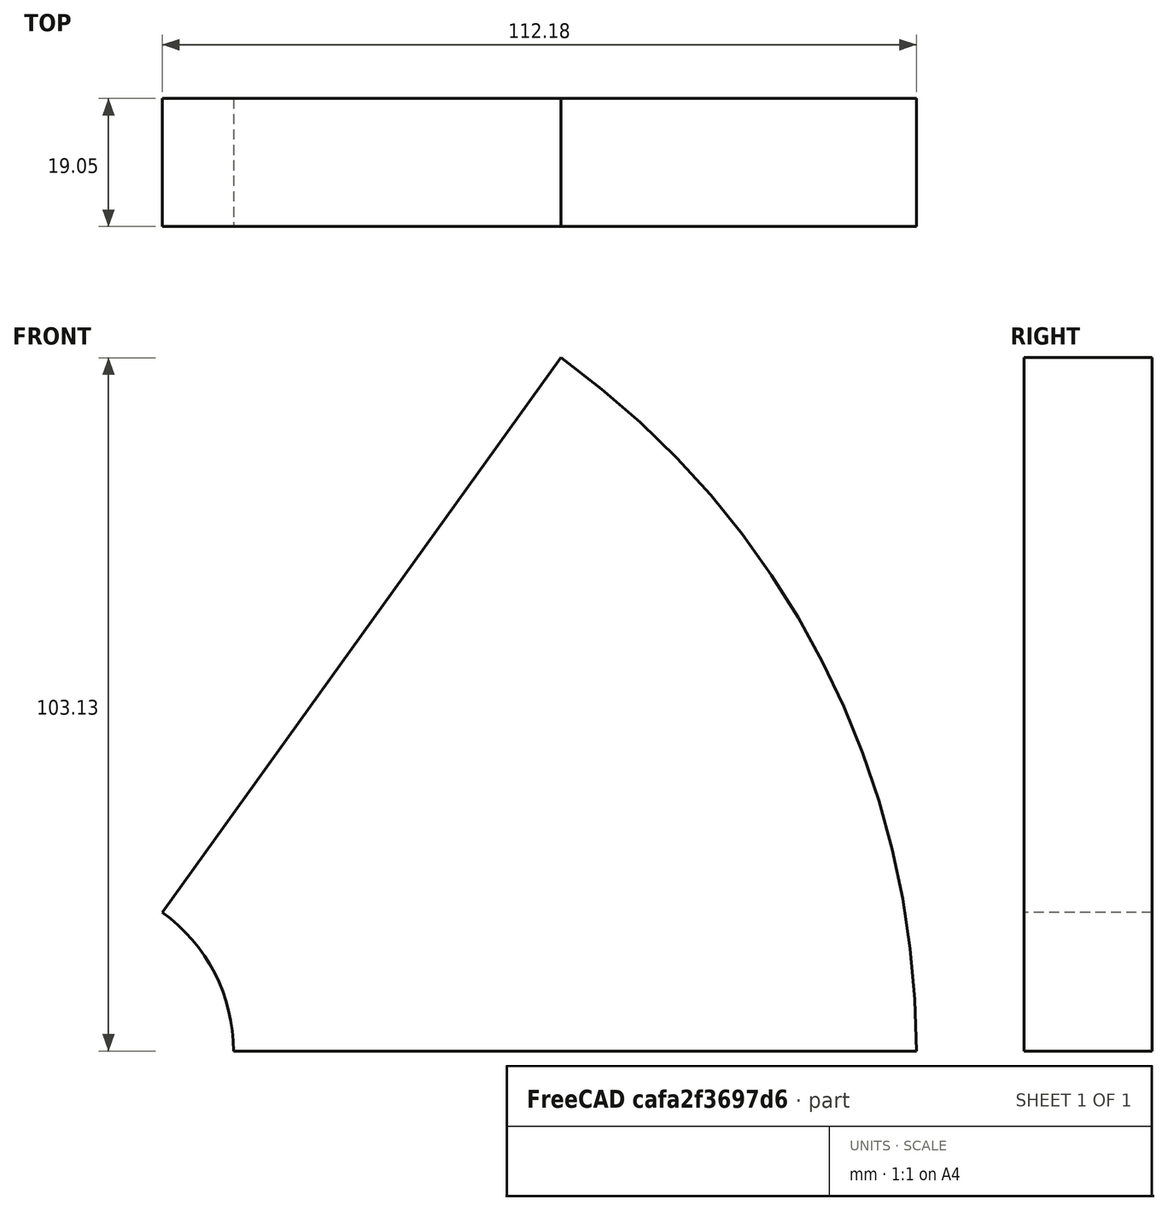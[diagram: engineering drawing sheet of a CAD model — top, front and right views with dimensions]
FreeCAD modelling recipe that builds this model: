
FCSTD DOCUMENT  (FreeCAD 0.19R24291 (Git))
Label: ArcWedge54.24Degrees
License: All rights reserved
LicenseURL: http://en.wikipedia.org/wiki/All_rights_reserved
objects: TechDraw::DrawViewDimension×4, TechDraw::DrawProjGroupItem×3, Sketcher::SketchObject×1, PartDesign::Pad×1, PartDesign::Body×1, TechDraw::DrawSVGTemplate×1, TechDraw::DrawProjGroup×1, TechDraw::DrawViewAnnotation×1, TechDraw::DrawPage×1
note: 4 computed .brp shape members not serialized (recipe doc carries the construction recipe); baked Part::Feature solids carry a one-line shape summary decoded from their .brp

FEATURE [Sketcher::SketchObject] Sketch
  FullyConstrained = true
  MapMode = 5
  Placement = pos=(0,0,0) rot=(1,0,0;1.5708rad)
  Support = -> [XZ_Plane]
  sketch-geometry (5):
    g0: ArcOfCircle CenterX=0 CenterY=0 CenterZ=0 NormalX=0 NormalY=0 NormalZ=1 AngleXU=0 Radius=127 StartAngle=0 EndAngle=0.947714
    g1: ArcOfCircle CenterX=0 CenterY=0 CenterZ=0 NormalX=0 NormalY=0 NormalZ=1 AngleXU=0 Radius=25.4 StartAngle=0 EndAngle=0.947714
    g2: LineSegment StartX=14.8219 StartY=20.6269 StartZ=0 EndX=74.1097 EndY=103.135 EndZ=0
    g3: LineSegment StartX=25.4 StartY=0 StartZ=0 EndX=127 EndY=0 EndZ=0
    g4: LineSegment StartX=0 StartY=0 StartZ=0 EndX=74.1097 EndY=103.135 EndZ=0
  constraints (14):
    c: PointOnObject(g0,g-1)
    c: Coincident(g1,g0)
    c: Coincident(g2,g1)
    c: Coincident(g2,g0)
    c: Coincident(g3,g0)
    c: Horizontal(g1,g0)
    c: Coincident(g3,g1)
    c: DistanceX(g0,g1) = 25.4
    c: Coincident(g0,g-1)
    c: DistanceX(g0,g0) = 127
    c: Coincident(g4,g0)
    c: Coincident(g4,g0)
    c: PointOnObject(g1,g4)
    c: Angle(g-1,g4) = 0.947714
FEATURE [PartDesign::Pad] Pad
  Direction = (1,1,1)
  Length = 19.05
  Length2 = 99.9998
  Placement = pos=(0,0,0) rot=(1,0,0;1.5708rad)
  Profile = -> Sketch
  Type = 0
FEATURE [PartDesign::Body] Body  label="BodyWedge54.24Degrees"
  Group = -> [Sketch,Pad]
  Origin = -> Origin
  Tip = -> Pad
FEATURE [TechDraw::DrawSVGTemplate] Template
  Height = 215.9
  Orientation = 1
  Width = 279.4
FEATURE [TechDraw::DrawProjGroupItem] ProjItem  label="Front"
  CoarseView = false
  Direction = (0,-1,0)
  Focus = 100
  HardHidden = false
  IsoCount = 0
  IsoHidden = false
  IsoVisible = false
  LockPosition = true
  Perspective = false
  Rotation = 0
  RotationVector = (1,0,0)
  ScaleType = 2
  SeamHidden = false
  SeamVisible = true
  SmoothHidden = false
  SmoothVisible = true
  Source = -> [Body]
  Type = 0
  X = 0
  XDirection = (1,0,0)
  Y = 0
FEATURE [TechDraw::DrawProjGroupItem] ProjItem001  label="Left"
  CoarseView = false
  Direction = (-1,-1e-16,0)
  Focus = 100
  HardHidden = false
  IsoCount = 0
  IsoHidden = false
  IsoVisible = false
  LockPosition = true
  Perspective = false
  Rotation = 0
  RotationVector = (1,0,0)
  ScaleType = 2
  SeamHidden = false
  SeamVisible = true
  SmoothHidden = false
  SmoothVisible = true
  Source = -> [Body]
  Type = 1
  X = 69.7737
  XDirection = (1e-16,-1,0)
  Y = 0
FEATURE [TechDraw::DrawProjGroupItem] ProjItem002  label="FrontTopLeft"
  CoarseView = false
  Direction = (-0.57735,-0.57735,0.57735)
  Focus = 100
  HardHidden = false
  IsoCount = 0
  IsoHidden = false
  IsoVisible = false
  LockPosition = true
  Perspective = false
  Rotation = 0
  RotationVector = (1,0,0)
  ScaleType = 2
  SeamHidden = false
  SeamVisible = true
  SmoothHidden = false
  SmoothVisible = true
  Source = -> [Body]
  Type = 6
  X = 137.752
  XDirection = (0.707107,-0.707107,0)
  Y = -4.17703
FEATURE [TechDraw::DrawProjGroup] ProjGroup
  Anchor = -> ProjItem
  AutoDistribute = true
  LockPosition = false
  ProjectionType = 0
  Rotation = 0
  ScaleType = 2
  Source = -> [Body]
  Views = -> [ProjItem,ProjItem001,ProjItem002]
  X = 76.0361
  Y = 107.95
  spacingX = 15.0114
  spacingY = 15.0114
FEATURE [TechDraw::DrawViewDimension] Dimension
  Arbitrary = false
  ArbitraryTolerances = false
  EqualTolerance = true
  FormatSpec = %.3f
  FormatSpecOverTolerance = %+.3f
  FormatSpecUnderTolerance = %+.3f
  Inverted = false
  LockPosition = false
  MeasureType = 1
  OverTolerance = 0
  References2D = -> [ProjItem001]
  Rotation = 0
  ScaleType = 2
  TheoreticalExact = false
  Type = 1
  UnderTolerance = 0
  X = -0.614164
  Y = -74.1235
FEATURE [TechDraw::DrawViewAnnotation] Annotation
  Font = osifont
  LineSpace = 80
  LockPosition = false
  MaxWidth = -1
  Rotation = 0
  ScaleType = 2
  Text = Wedge 54.24 degrees.
  TextSize = 5.0038
  TextStyle = 0
  X = 61.0716
  Y = 176.095
FEATURE [TechDraw::DrawViewDimension] Dimension001
  Arbitrary = false
  ArbitraryTolerances = false
  EqualTolerance = true
  FormatSpec = %.3f
  FormatSpecOverTolerance = %+.3f
  FormatSpecUnderTolerance = %+.3f
  Inverted = false
  LockPosition = false
  MeasureType = 1
  OverTolerance = 0
  References2D = -> [ProjItem]
  Rotation = 0
  ScaleType = 2
  TheoreticalExact = false
  Type = 6
  UnderTolerance = 0
  X = 0
  Y = 0
FEATURE [TechDraw::DrawViewDimension] Dimension002
  Arbitrary = false
  ArbitraryTolerances = false
  EqualTolerance = true
  FormatSpec = %.3f
  FormatSpecOverTolerance = %+.3f
  FormatSpecUnderTolerance = %+.3f
  Inverted = false
  LockPosition = false
  MeasureType = 1
  OverTolerance = 0
  References2D = -> [ProjItem]
  Rotation = 0
  ScaleType = 2
  TheoreticalExact = false
  Type = 1
  UnderTolerance = 0
  X = 2.56302
  Y = -56.4741
FEATURE [TechDraw::DrawViewDimension] Dimension003
  Arbitrary = false
  ArbitraryTolerances = false
  EqualTolerance = true
  FormatSpec = %.3f
  FormatSpecOverTolerance = %+.3f
  FormatSpecUnderTolerance = %+.3f
  Inverted = false
  LockPosition = false
  MeasureType = 1
  OverTolerance = 0
  References2D = -> [ProjItem]
  Rotation = 0
  ScaleType = 2
  TheoreticalExact = false
  Type = 1
  UnderTolerance = 0
  X = 1.36301
  Y = -66.8783
FEATURE [TechDraw::DrawPage] Page  label="PageWedge54.24Degrees"
  KeepUpdated = true
  NextBalloonIndex = 1
  ProjectionType = 0
  Template = -> Template
  Views = -> [ProjGroup,Dimension,Annotation,Dimension001,Dimension002,Dimension003]
